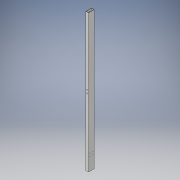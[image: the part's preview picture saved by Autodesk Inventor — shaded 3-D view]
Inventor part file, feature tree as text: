
AUTODESK INVENTOR PART (.ipt)
format: ipt  version: 2017 (Build 210142000, 142)  size: 138,240 bytes
history: native  units: in
note: dims shown in document units (in); Inventor stores cm internally (conversion verified against a paired STEP export)
features: sketch x4, extrude x3, hole x1
ambient origin geometry x8: Origin, YZ Plane, XZ Plane, XY Plane, X Axis, Y Axis, Z Axis, Center Point
bodies: Solid1 (feature_tree)
feature tree (8):
  extrude  "Extrusion1"  Depth=2.0in
  extrude  "Extrusion2"  Depth=1.75in
  extrude  "Extrusion3"  Depth=0.125in
  hole  "Hole1"  [1 undecoded]
  sketch  "Sketch2"  dims[d2=1.0in d3=2.0in]
  sketch  "Sketch3"  dims[d4=0.75in d5=1.75in]
  sketch  "Sketch4"  dims[d6=0.125in d7=0.125in]
  sketch  "Sketch5"  dims[d8=48.0in d9=0.0in d10=48.0in d11=24.0in d12=0.5in d13=0.25in d14=48.0in d15=0.0in d16=1.125in d17=1.125in d18=0.25in d19=0.0in d20=4.5in d21=0.5in d22=0.125in d24=0.125in d25=0.75in d26=0.375in d27=0.25in d28=0.5635in d29=0.125in d30=0.8108in]
note: 1 required parameter value undecoded (feature->parameter linkage not recoverable at this tier; creation-order binding heuristic only, values carry confidence <= 0.55)
